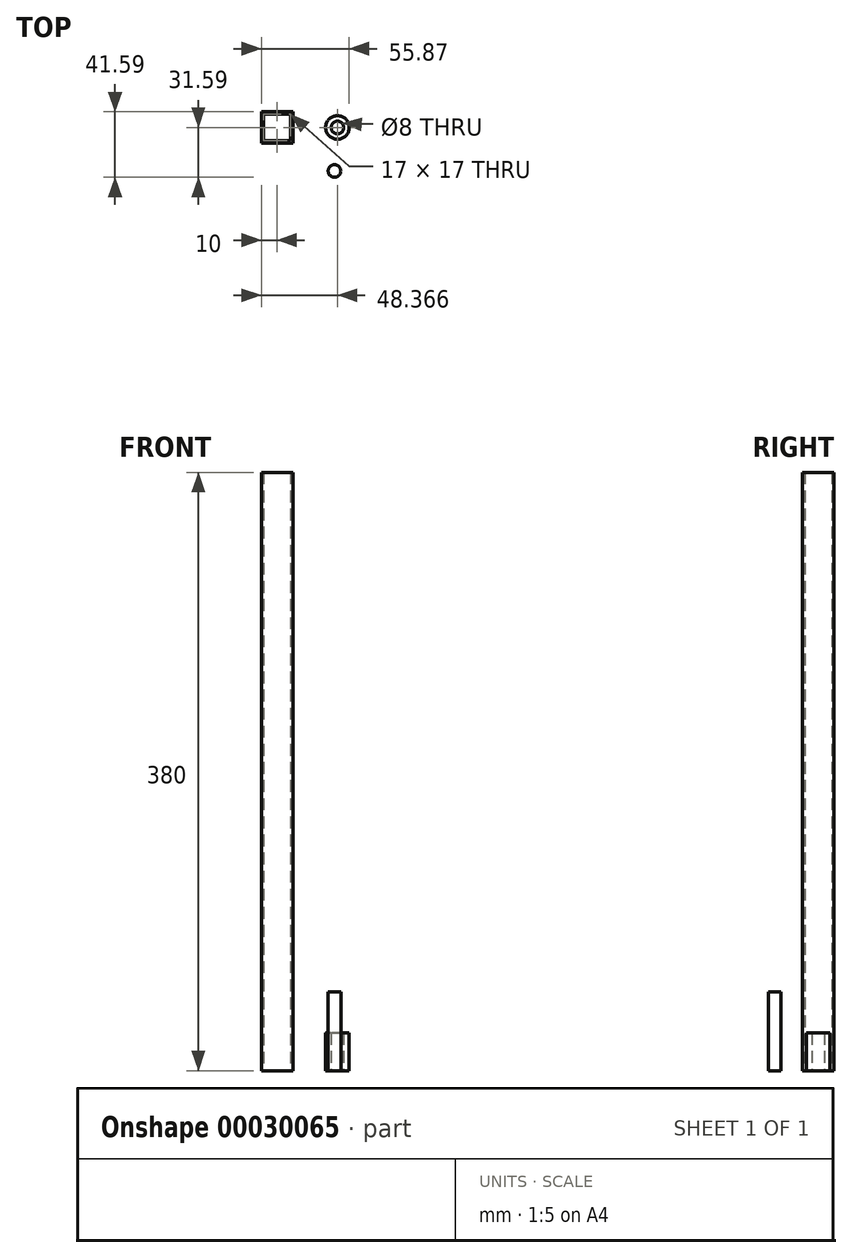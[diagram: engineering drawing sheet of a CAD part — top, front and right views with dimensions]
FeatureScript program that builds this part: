
annotation { "Feature Type Name" : "Feature", "Feature Type Description" : "" }
export const myFeature = defineFeature(function(context is Context, id is Id, definition is map)
    precondition{}
    {
        {
            var Q0;
            Q0=qCreatedBy(makeId("Top.planeOp"),FACE);
            var sketch = newSketch(context, id + "F0", { "sketchPlane" : qUnion([Q0])});
            skLineSegment(sketch, "E0.rect.bottom", {"start": v(8.5, 8.5) * mm, "end": v(-8.5, 8.5) * mm});
            skLineSegment(sketch, "E0.rect.top", {"start": v(8.5, -8.5) * mm, "end": v(-8.5, -8.5) * mm});
            skLineSegment(sketch, "E0.rect.left", {"start": v(8.5, 8.5) * mm, "end": v(8.5, -8.5) * mm});
            skLineSegment(sketch, "E0.rect.right", {"start": v(-8.5, 8.5) * mm, "end": v(-8.5, -8.5) * mm});
            skPoint(sketch, "E0.rect.middle", {"position": v(0, 0) * mm});
            skLineSegment(sketch, "E1.rect.bottom", {"start": v(10, 10) * mm, "end": v(-10, 10) * mm});
            skLineSegment(sketch, "E1.rect.top", {"start": v(10, -10) * mm, "end": v(-10, -10) * mm});
            skLineSegment(sketch, "E1.rect.left", {"start": v(10, 10) * mm, "end": v(10, -10) * mm});
            skLineSegment(sketch, "E1.rect.right", {"start": v(-10, 10) * mm, "end": v(-10, -10) * mm});
            skSolve(sketch);
        }
        {
            var Q0;
            Q0 = qSketchRegion(id + "F0", true);
            extrude(context, id + "F1", {"entities" : qUnion([Q0]), "depth" : 380 * mm});
        }
        {
            var Q0;
            Q0=qCreatedBy(makeId("Top.planeOp"),FACE);
            var sketch = newSketch(context, id + "F2", { "sketchPlane" : qUnion([Q0])});
            skCircle(sketch, "E2", {"center": v(38.37, 0) * mm, "radius": 7.5 * mm});
            skCircle(sketch, "E3", {"center": v(38.37, 0) * mm, "radius": 4 * mm});
            skSolve(sketch);
        }
        {
            var Q0;
            Q0 = qSketchRegion(id + "F2", true);
            extrude(context, id + "F3", {"entities" : qUnion([Q0]), "depth" : 24 * mm});
        }
        {
            var Q0;
            Q0=qCreatedBy(makeId("Top.planeOp"),FACE);
            var sketch = newSketch(context, id + "F4", { "sketchPlane" : qUnion([Q0])});
            skCircle(sketch, "E4", {"center": v(36.48, -27.6) * mm, "radius": 4 * mm});
            skSolve(sketch);
        }
        {
            var Q0;
            Q0 = qSketchRegion(id + "F4", true);
            extrude(context, id + "F5", {"entities" : qUnion([Q0]), "depth" : 50 * mm});
        }
    });
